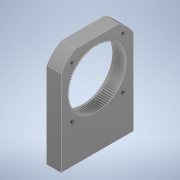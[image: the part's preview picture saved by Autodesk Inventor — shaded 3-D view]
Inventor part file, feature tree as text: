
AUTODESK INVENTOR PART (.ipt)
format: ipt  version: 2022 (Build 260153000, 153)  size: 684,544 bytes
history: mixed  units: in
note: dims shown in document units (in); Inventor stores cm internally (conversion verified against a paired STEP export)
features: sketch x7, extrude x6, other x1, imported_body x1
ambient origin geometry x8: Origin, YZ Plane, XZ Plane, XY Plane, X Axis, Y Axis, Z Axis, Center Point
bodies: Solid1 (imported_parasolid)
feature tree (15):
  extrude  "Extrusion1"  Depth=0.3937in TaperAngle=0.0deg
  extrude  "Extrusion2"  Depth=0.3937in
  extrude  "Extrusion3"  Depth=0.1181in
  sketch  "Sketch5"  dims[d10=0.0in d11=0.0in d12=0.315in d13=0.0in]
  extrude  "Extrusion4"  Depth=0.315in TaperAngle=0.0deg
  extrude  "Extrusion5"  TaperAngle=0.0deg  [1 undecoded]
  extrude  "Extrusion6"  [1 undecoded]
  sketch  "Sketch2"  dims[d1=0.2756in d2=0.0in d3=0.3937in d4=0.0in]
  sketch  "Sketch3"  dims[d5=0.3937in d6=0.0in d7=0.1181in]
  sketch  "Sketch4"  dims[d8=0.1181in d9=0.1181in]
  sketch  "Sketch6"  dims[d14=1.378in d15=0.0in d16=0.0in]
  sketch  "Sketch7"
  sketch  "Sketch8"
  other  "96_Teeth_Gear.STEP"
  imported_body  NMx_Import_Brep_tag  [imported B-rep: ~397 faces, bbox_mm=[12.0, 83.027756, 60.0]]
note: 2 required parameter values undecoded (feature->parameter linkage not recoverable at this tier; creation-order binding heuristic only, values carry confidence <= 0.55)
